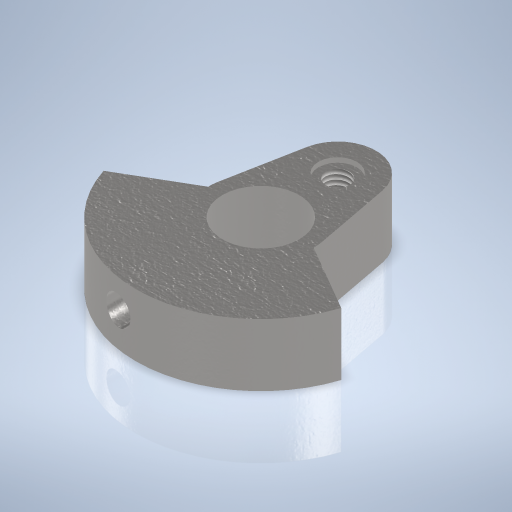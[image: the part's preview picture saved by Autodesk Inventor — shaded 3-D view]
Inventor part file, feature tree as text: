
AUTODESK INVENTOR PART (.ipt)
format: ipt  version: 2024 (Build 280153000, 153)  size: 338,944 bytes
history: native  units: mm
features: sketch x4, extrude x2, hole x2, projected_geometry x2, plane x1
ambient origin geometry x8: Origin, YZ Plane, XZ Plane, XY Plane, X Axis, Y Axis, Z Axis, Center Point
bodies: Volumenkörper1 (feature_tree)
feature tree (11):
  extrude  "Extrusion1"  Depth=11.0mm
  extrude  "Extrusion2"  Depth=4.0mm
  hole  "Bohrung1"  [1 undecoded]
  plane  "Arbeitsebene1"
  hole  "Bohrung2"  [1 undecoded]
  sketch  "Skizze1"  dims[d2=26.0mm d3=11.0mm]
  sketch  "Skizze2"  dims[d4=4.0mm d5=4.0mm]
  projected_geometry  "Projizierte Kontur1"
  sketch  "Skizze3"  dims[d6=8.0mm d7=6.5mm d8=0.0mm]
  sketch  "Skizze4"  dims[d9=8.0mm d10=0.0mm d11=0.0mm d12=8.0mm d13=2.459mm d14=6.0mm d15=4.0mm d16=0.5mm d17=90.0deg d18=9.0mm d19=20.594885mm d20=0.0mm d25=3.0mm d26=14.456832mm d27=3.0mm d28=8.0mm d29=4.0mm d30=0.5mm d31=90.0deg d32=8.0mm d33=0.0mm]
  projected_geometry  "Projizierte Kontur2"
note: 2 required parameter values undecoded (feature->parameter linkage not recoverable at this tier; creation-order binding heuristic only, values carry confidence <= 0.55)
